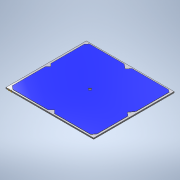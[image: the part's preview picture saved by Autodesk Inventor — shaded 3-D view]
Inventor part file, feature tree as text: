
AUTODESK INVENTOR PART (.ipt)
format: ipt  version: 2020 (Build 240168000, 168)  size: 146,944 bytes
history: native  units: mm
features: extrude x2, sketch x2, other x1
ambient origin geometry x8: Origin, YZ Plane, XZ Plane, XY Plane, X Axis, Y Axis, Z Axis, Center Point
bodies: Body1 (feature_tree)
feature tree (5):
  other  "Sólido1"
  extrude  "Extrusión1"  Depth=180.0mm
  extrude  "Extrusión2"  TaperAngle=135.0deg  [1 undecoded]
  sketch  "Boceto1"  dims[d2=165.0mm d3=180.0mm]
  sketch  "Boceto3"  dims[d4=5.0mm d5=0.0mm d7=135.0deg d8=135.0deg d9=45.0deg d10=1.0mm d11=0.0mm]
note: 1 required parameter value undecoded (feature->parameter linkage not recoverable at this tier; creation-order binding heuristic only, values carry confidence <= 0.55)
